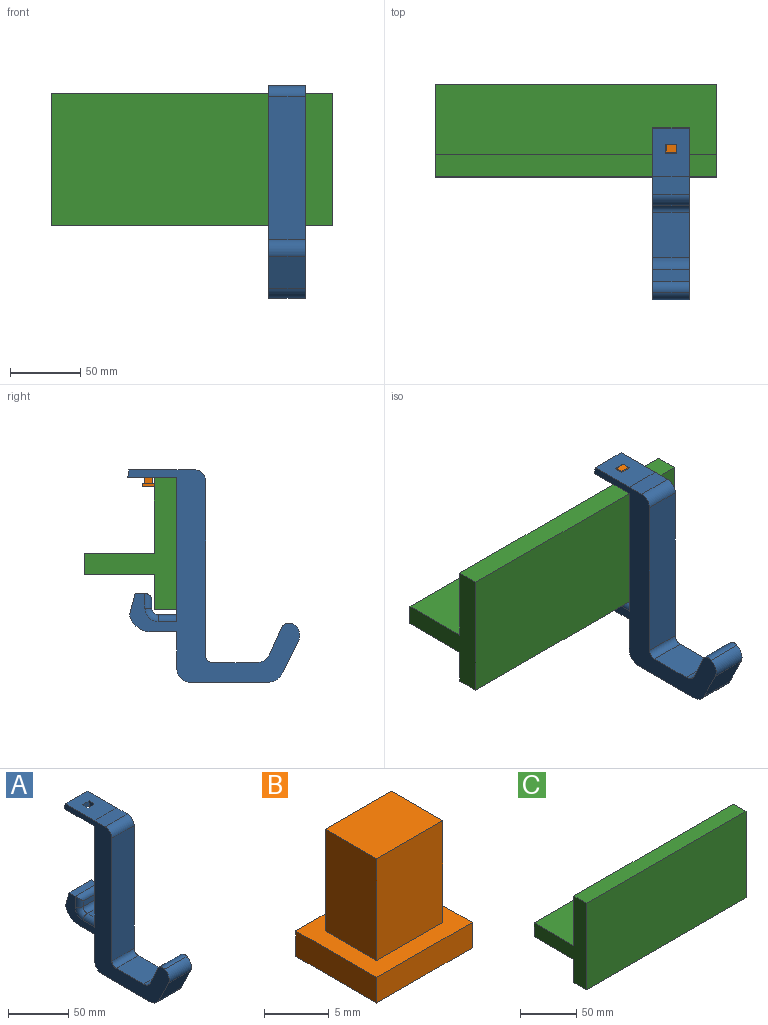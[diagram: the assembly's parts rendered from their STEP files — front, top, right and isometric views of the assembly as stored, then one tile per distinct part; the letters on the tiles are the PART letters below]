
ASSEMBLY  parts=3 mates=4
PART A: 38 faces, bbox 26x122.4x151.1 mm
  f0: plane 35x26mm, normal (0,0,-1), area 858mm2, adj f6,f7,f16,f17,f26,f27,f28,f29
  f1: plane 34.2x26mm, normal (0,0,1), area 837.2mm2, adj f7,f8,f16,f17,f26,f27,f28,f29
  f2: plane 26x15.3mm, normal (0,0.97,0.26), area 411.7mm2, adj f3,f16,f17,f18
  f3: plane 26x7.02mm, normal (0,-0.03,1), area 182.5mm2, adj f2,f16,f17,f31,f33,f35
  f4: plane 16.41x5.53mm, normal (0,-1,0), area 90.8mm2, adj f31,f33,f34,f35
  f5: plane 16.41x13.21mm, normal (0,0,1), area 216.7mm2, adj f6,f30,f34,f37
  f6: plane 102.29x26mm, normal (0,1,0), area 2544.9mm2, adj f0,f5,f16,f17,f30,f37
  f7: plane 26x5.5mm, normal (0,0.99,0.14), area 144.5mm2, adj f0,f1,f16,f17
  f8: plane 26x12.4mm, normal (0,0.01,1), area 322.4mm2, adj f1,f16,f17,f19
  f9: plane 124.29x26mm, normal (0,-1,0), area 3231.5mm2, adj f16,f17,f19,f25
  f10: plane 31.93x26mm, normal (0,0,1), area 830.1mm2, adj f16,f17,f24,f25
  f11: plane 26x18.8mm, normal (0,0.91,0.41), area 534.8mm2, adj f16,f17,f23,f24
  f12: plane 26x22.93mm, normal (0,-0.9,-0.44), area 663.8mm2, adj f16,f17,f21,f22
  f13: plane 55.51x26mm, normal (0,0,-1), area 1443.4mm2, adj f16,f17,f20,f21
  f14: plane 26.76x26mm, normal (0,1,0), area 695.6mm2, adj f15,f16,f17,f20
  f15: plane 26x18.89mm, normal (0,0,-1), area 491.1mm2, adj f14,f16,f17,f18
  f16: plane 151.08x122.36mm, normal (1,0,0), area 4811.6mm2, adj f0,f1,f2,f3,f6,f7,f8,f9
  f17: plane 151.08x122.36mm, normal (-1,0,0), area 4811.6mm2, adj f0,f1,f2,f3,f6,f7,f8,f9
  f18: cylinder r=15.21mm len=26mm, axis (1,0,0), area 537.1mm2, adj f2,f15,f16,f17
  f19: cylinder r=7.79mm len=26mm, axis (-1,0,0), area 320.6mm2, adj f8,f9,f16,f17
  f20: cylinder r=9.17mm len=26mm, axis (-1,0,0), area 374.7mm2, adj f13,f14,f16,f17
  f21: cylinder r=11.75mm len=26mm, axis (-1,0,0), area 340.8mm2, adj f12,f13,f16,f17
  f22: cylinder r=8.82mm len=26mm, axis (-1,0,0), area 366mm2, adj f12,f16,f17,f23
  f23: cylinder r=6.1mm len=26mm, axis (-1,0,0), area 250.9mm2, adj f11,f16,f17,f22
  f24: cylinder r=9.34mm len=26mm, axis (-1,0,0), area 280mm2, adj f10,f11,f16,f17
  f25: cylinder r=5mm len=26mm, axis (1,0,0), area 204.2mm2, adj f9,f10,f16,f17
  f26: plane 8x5.5mm, normal (0,-1,0), area 44mm2, adj f0,f1,f27,f29
  f27: plane 6.5x5.5mm, normal (1,0,0), area 35.8mm2, adj f0,f1,f26,f28
  f28: plane 8x5.5mm, normal (0,1,0), area 44mm2, adj f0,f1,f27,f29
  f29: plane 6.5x5.5mm, normal (-1,0,0), area 35.8mm2, adj f0,f1,f26,f28
  f30: cylinder r=4.79mm len=13.21mm, axis (0,-1,0), area 99.4mm2, adj f5,f6,f17,f32
  f31: cylinder r=4.79mm len=10.33mm, axis (0,0,-1), area 64.7mm2, adj f3,f4,f17,f32,f33
  f32: torus R=9.59mm, axis (1,0,0), area 77.3mm2, adj f17,f30,f31,f34
  f33: cylinder r=4.79mm len=26mm, axis (-1,0,0), area 166.3mm2, adj f3,f4,f31,f35
  f34: cylinder r=4.79mm len=16.41mm, axis (-1,0,0), area 123.6mm2, adj f4,f5,f32,f36
  f35: cylinder r=4.79mm len=10.33mm, axis (0,0,1), area 64.7mm2, adj f3,f4,f16,f33,f36
  f36: torus R=9.59mm, axis (1,0,0), area 77.3mm2, adj f16,f34,f35,f37
  f37: cylinder r=4.79mm len=13.21mm, axis (0,1,0), area 99.4mm2, adj f5,f6,f16,f36
PART B: 11 faces, bbox 10.4x8.8x12 mm
  f0: plane 9.6x5.6mm, normal (-1,0,0), area 53.8mm2, adj f1,f3,f4,f9
  f1: plane 9.6x7.2mm, normal (0,-1,0), area 69.1mm2, adj f0,f2,f4,f9
  f2: plane 9.6x5.6mm, normal (1,0,0), area 53.8mm2, adj f1,f3,f4,f9
  f3: plane 9.6x7.2mm, normal (0,1,0), area 69.1mm2, adj f0,f2,f4,f9
  f4: plane 7.2x5.6mm, normal (0,0,1), area 40.3mm2, adj f0,f1,f2,f3
  f5: plane 8.8x2.4mm, normal (-1,0,0), area 21.1mm2, adj f6,f8,f9,f10
  f6: plane 10.4x2.4mm, normal (0,-1,0), area 25mm2, adj f5,f7,f9,f10
  f7: plane 8.8x2.4mm, normal (1,0,0), area 21.1mm2, adj f6,f8,f9,f10
  f8: plane 10.4x2.4mm, normal (0,1,0), area 25mm2, adj f5,f7,f9,f10
  f9: plane 10.4x8.8mm, normal (0,0,1), area 51.2mm2, adj f0,f1,f2,f3,f5,f6,f7,f8
  f10: plane 10.4x8.8mm, normal (0,0,-1), area 91.5mm2, adj f5,f6,f7,f8
PART C: 10 faces, bbox 200x66x94 mm
  f0: plane 200x25mm, normal (0,1,0), area 5000mm2, adj f2,f3,f4,f7
  f1: plane 200x16mm, normal (0,0,1), area 3200mm2, adj f2,f4,f5,f6
  f2: plane 94x66mm, normal (-1,0,0), area 2254mm2, adj f0,f1,f3,f5,f6,f7,f8,f9
  f3: plane 200x16mm, normal (0,0,-1), area 3200mm2, adj f0,f2,f4,f5
  f4: plane 94x66mm, normal (1,0,0), area 2254mm2, adj f0,f1,f3,f5,f6,f7,f8,f9
  f5: plane 200x94mm, normal (0,-1,0), area 18800mm2, adj f1,f2,f3,f4
  f6: plane 200x54mm, normal (0,1,0), area 10800mm2, adj f1,f2,f4,f8
  f7: plane 200x50mm, normal (0,0,-1), area 10000mm2, adj f0,f2,f4,f9
  f8: plane 200x50mm, normal (0,0,1), area 10000mm2, adj f2,f4,f6,f9
  f9: plane 200x15mm, normal (0,1,0), area 3000mm2, adj f2,f4,f7,f8
PLACE A t=(59.57,-25.81,12.28)mm
PLACE B t=(73.02,-22,63.95)mm
PLACE C t=(-34.33,-27.81,17.72)mm fixed
MATE planar A.f6 <-> C.f5  axis (0,1,0) through (72.57,-43.81,21.44)mm
MATE planar A.f0 <-> C.f1  axis (0,0,-1) through (72.57,-26.46,70.38)mm
MATE planar B.f2 <-> A.f29  axis (1,0,0) through (76.57,-23.41,71.15)mm
MATE planar B.f3 <-> A.f26  axis (0,1,0) through (72.97,-20.61,71.15)mm
